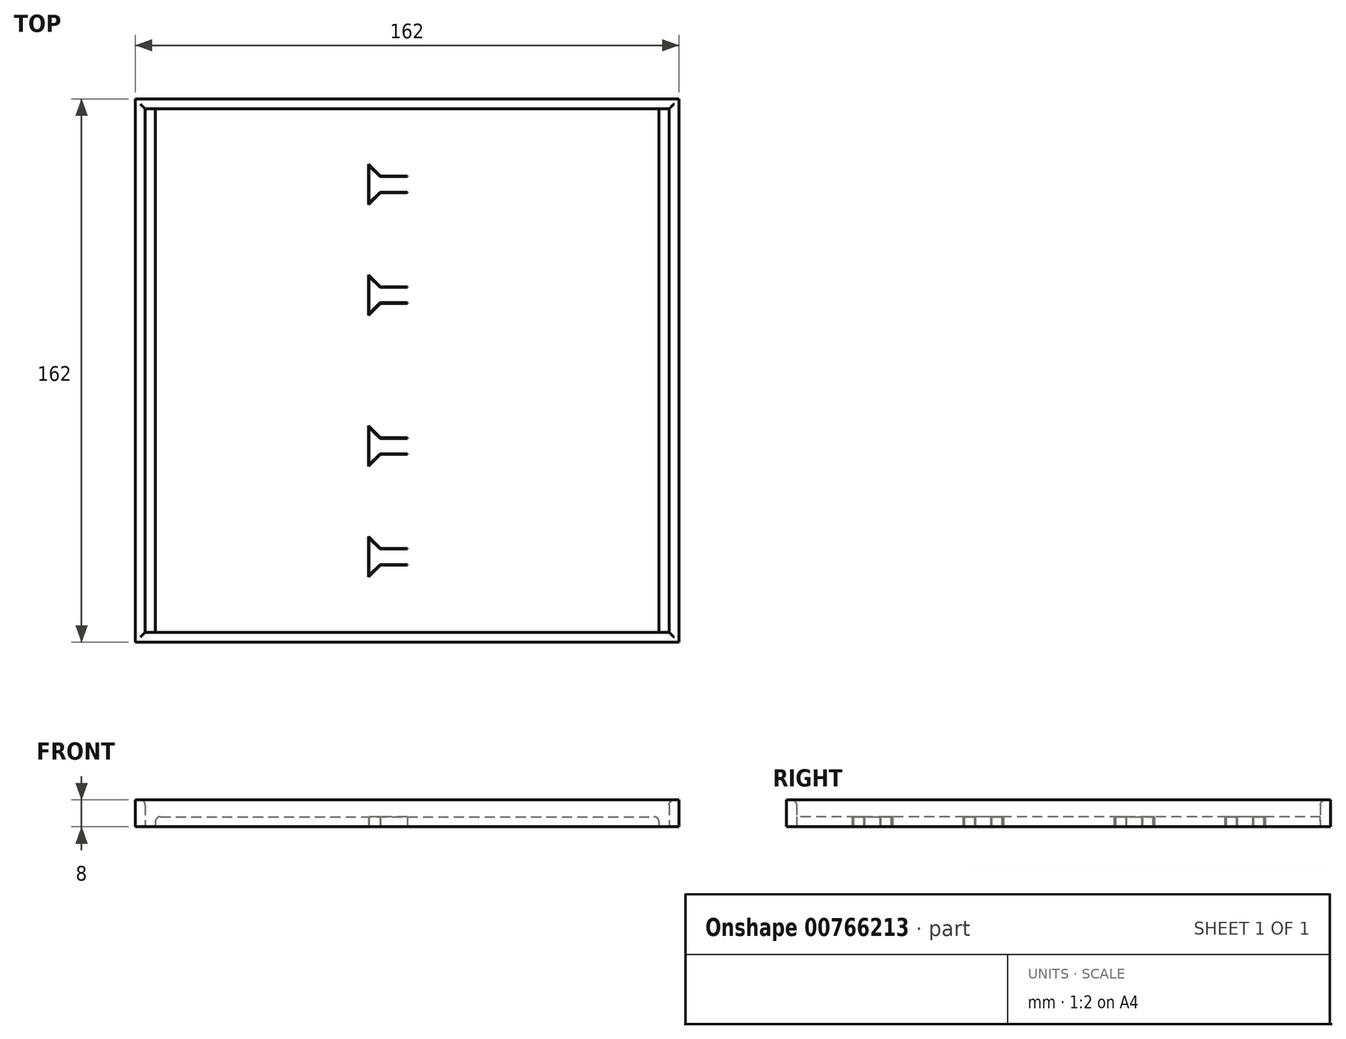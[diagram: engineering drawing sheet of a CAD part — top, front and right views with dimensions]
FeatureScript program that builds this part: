
annotation { "Feature Type Name" : "Feature", "Feature Type Description" : "" }
export const myFeature = defineFeature(function(context is Context, id is Id, definition is map)
    precondition{}
    {
        {
            var Q0;
            Q0=qCreatedBy(makeId("Top.planeOp"),FACE);
            var sketch = newSketch(context, id + "F0", { "sketchPlane" : qUnion([Q0])});
            skLineSegment(sketch, "E0.bottom", {"start": v(-39, 39) * mm, "end": v(39, 39) * mm});
            skLineSegment(sketch, "E0.top", {"start": v(-39, -39) * mm, "end": v(39, -39) * mm, "construction": true});
            skLineSegment(sketch, "E0.left", {"start": v(-39, 39) * mm, "end": v(-39, -39) * mm});
            skLineSegment(sketch, "E0.right", {"start": v(39, 39) * mm, "end": v(39, -39) * mm, "construction": true});
            skPoint(sketch, "E0.middle", {"position": v(0, 0) * mm});
            skLineSegment(sketch, "E1", {"start": v(-39, -39) * mm, "end": v(-42, -39) * mm, "construction": true});
            skLineSegment(sketch, "E2", {"start": v(-42, -39) * mm, "end": v(-42, 42) * mm});
            skLineSegment(sketch, "E3", {"start": v(-42, 42) * mm, "end": v(39, 42) * mm});
            skLineSegment(sketch, "E4", {"start": v(39, 42) * mm, "end": v(39, 39) * mm, "construction": true});
            skLineSegment(sketch, "E5.MirrorCS", {"start": v(-39, -117) * mm, "end": v(39, -117) * mm});
            skLineSegment(sketch, "E6.MirrorCS", {"start": v(-42, -120) * mm, "end": v(39, -120) * mm});
            skLineSegment(sketch, "E7.MirrorCS", {"start": v(-39, -117) * mm, "end": v(-39, -39) * mm});
            skLineSegment(sketch, "E8.MirrorCS", {"start": v(-42, -39) * mm, "end": v(-42, -120) * mm});
            skLineSegment(sketch, "E9.MirrorCS", {"start": v(117, -117) * mm, "end": v(117, -39) * mm});
            skLineSegment(sketch, "E10.MirrorCS", {"start": v(117, 39) * mm, "end": v(117, -39) * mm});
            skLineSegment(sketch, "E11.MirrorCS", {"start": v(120, -39) * mm, "end": v(120, 42) * mm});
            skLineSegment(sketch, "E12.MirrorCS", {"start": v(120, -39) * mm, "end": v(120, -120) * mm});
            skLineSegment(sketch, "E13.MirrorCS", {"start": v(120, 42) * mm, "end": v(39, 42) * mm});
            skLineSegment(sketch, "E14.MirrorCS", {"start": v(117, 39) * mm, "end": v(39, 39) * mm});
            skLineSegment(sketch, "E15.MirrorCS", {"start": v(117, -117) * mm, "end": v(39, -117) * mm});
            skLineSegment(sketch, "E16.MirrorCS", {"start": v(120, -120) * mm, "end": v(39, -120) * mm});
            skLineSegment(sketch, "E17", {"start": v(39, 42) * mm, "end": v(39, -120) * mm});
            skPoint(sketch, "E18", {"position": v(39, 19) * mm});
            skPoint(sketch, "E19", {"position": v(39, 14) * mm});
            skPoint(sketch, "E20", {"position": v(39, 0) * mm});
            skLineSegment(sketch, "E21", {"start": v(39, 19) * mm, "end": v(31, 19) * mm});
            skLineSegment(sketch, "E22", {"start": v(31, 19) * mm, "end": v(27.46, 22.54) * mm});
            skLineSegment(sketch, "E23", {"start": v(27.46, 22.54) * mm, "end": v(27.46, 10.46) * mm});
            skLineSegment(sketch, "E24", {"start": v(27.46, 10.46) * mm, "end": v(31, 14) * mm});
            skLineSegment(sketch, "E25", {"start": v(31, 14) * mm, "end": v(39, 14) * mm});
            skLineSegment(sketch, "E26", {"start": v(0, 0) * mm, "end": v(39, 0) * mm, "construction": true});
            skLineSegment(sketch, "E27.MirrorCS", {"start": v(31, -14) * mm, "end": v(39, -14) * mm});
            skLineSegment(sketch, "E28.MirrorCS", {"start": v(27.46, -10.46) * mm, "end": v(31, -14) * mm});
            skLineSegment(sketch, "E29.MirrorCS", {"start": v(27.46, -22.54) * mm, "end": v(27.46, -10.46) * mm});
            skLineSegment(sketch, "E30.MirrorCS", {"start": v(31, -19) * mm, "end": v(27.46, -22.54) * mm});
            skLineSegment(sketch, "E31.MirrorCS", {"start": v(39, -19) * mm, "end": v(31, -19) * mm});
            skLineSegment(sketch, "E32.MirrorCS", {"start": v(39, -59) * mm, "end": v(31, -59) * mm});
            skLineSegment(sketch, "E33.MirrorCS", {"start": v(31, -59) * mm, "end": v(27.46, -55.46) * mm});
            skLineSegment(sketch, "E34.MirrorCS", {"start": v(27.46, -55.46) * mm, "end": v(27.46, -67.54) * mm});
            skLineSegment(sketch, "E35.MirrorCS", {"start": v(27.46, -67.54) * mm, "end": v(31, -64) * mm});
            skLineSegment(sketch, "E36.MirrorCS", {"start": v(31, -64) * mm, "end": v(39, -64) * mm});
            skLineSegment(sketch, "E37.MirrorCS", {"start": v(31, -92) * mm, "end": v(39, -92) * mm});
            skLineSegment(sketch, "E38.MirrorCS", {"start": v(39, -97) * mm, "end": v(31, -97) * mm});
            skLineSegment(sketch, "E39.MirrorCS", {"start": v(31, -97) * mm, "end": v(27.46, -100.54) * mm});
            skLineSegment(sketch, "E40.MirrorCS", {"start": v(27.46, -100.54) * mm, "end": v(27.46, -88.46) * mm});
            skLineSegment(sketch, "E41.MirrorCS", {"start": v(27.46, -88.46) * mm, "end": v(31, -92) * mm});
            skLineSegment(sketch, "E42", {"start": v(-36, 39) * mm, "end": v(-36, -117) * mm});
            skLineSegment(sketch, "E43.MirrorCS", {"start": v(114, 39) * mm, "end": v(114, -117) * mm});
            skLineSegment(sketch, "E44.0", {"start": v(30.92, 14.2) * mm, "end": v(39, 14.2) * mm});
            skLineSegment(sketch, "E44.1", {"start": v(39, 18.8) * mm, "end": v(30.92, 18.8) * mm});
            skLineSegment(sketch, "E44.2", {"start": v(30.92, 18.8) * mm, "end": v(27.66, 22.05) * mm});
            skLineSegment(sketch, "E44.3", {"start": v(27.66, 22.05) * mm, "end": v(27.66, 10.95) * mm});
            skLineSegment(sketch, "E44.4", {"start": v(27.66, 10.95) * mm, "end": v(30.92, 14.2) * mm});
            skLineSegment(sketch, "E45.MirrorCS", {"start": v(30.92, -14.2) * mm, "end": v(39, -14.2) * mm});
            skLineSegment(sketch, "E46.MirrorCS", {"start": v(27.66, -10.95) * mm, "end": v(30.92, -14.2) * mm});
            skLineSegment(sketch, "E47.MirrorCS", {"start": v(27.66, -22.05) * mm, "end": v(27.66, -10.95) * mm});
            skLineSegment(sketch, "E48.MirrorCS", {"start": v(30.92, -18.8) * mm, "end": v(27.66, -22.05) * mm});
            skLineSegment(sketch, "E49.MirrorCS", {"start": v(39, -18.8) * mm, "end": v(30.92, -18.8) * mm});
            skLineSegment(sketch, "E50.MirrorCS", {"start": v(39, -59.2) * mm, "end": v(30.92, -59.2) * mm});
            skLineSegment(sketch, "E51.MirrorCS", {"start": v(30.92, -59.2) * mm, "end": v(27.66, -55.95) * mm});
            skLineSegment(sketch, "E52.MirrorCS", {"start": v(27.66, -55.95) * mm, "end": v(27.66, -67.05) * mm});
            skLineSegment(sketch, "E53.MirrorCS", {"start": v(30.92, -63.8) * mm, "end": v(39, -63.8) * mm});
            skLineSegment(sketch, "E54.MirrorCS", {"start": v(27.66, -67.05) * mm, "end": v(30.92, -63.8) * mm});
            skLineSegment(sketch, "E55.MirrorCS", {"start": v(30.92, -92.2) * mm, "end": v(39, -92.2) * mm});
            skLineSegment(sketch, "E56.MirrorCS", {"start": v(27.66, -88.95) * mm, "end": v(30.92, -92.2) * mm});
            skLineSegment(sketch, "E57.MirrorCS", {"start": v(27.66, -100.05) * mm, "end": v(27.66, -88.95) * mm});
            skLineSegment(sketch, "E58.MirrorCS", {"start": v(30.92, -96.8) * mm, "end": v(27.66, -100.05) * mm});
            skLineSegment(sketch, "E59.MirrorCS", {"start": v(39, -96.8) * mm, "end": v(30.92, -96.8) * mm});
            skSolve(sketch);
        }
        {
            var Q0;
            {var subQ1=sQuery(id+"F0.wireOp",EDGE,"E0.bottom");Q0=makeQuery(id+"F0.imprint","IMPRINT",FACE,{"disambiguationData":[TD([[makeQuery(id+"F0.imprint","IMPRINT",EDGE,{"derivedFrom":subQ1}),1.0]])]});}
            extrude(context, id + "F1", {"entities" : qUnion([Q0]), "depth" : 8 * mm, "offsetDistance" : 25 * mm});
        }
        {
            var Q0;
            {var subQ9=sQuery(id+"F0.wireOp",EDGE,"E21");Q0=makeQuery(id+"F0.imprint","IMPRINT",FACE,{"disambiguationData":[TD([[makeQuery(id+"F0.imprint","IMPRINT",EDGE,{"derivedFrom":subQ9}),-1.0]])]});}
            extrude(context, id + "F2", {"entities" : qUnion([Q0]), "operationType" : NewBodyOperationType.ADD, "depth" : 3 * mm, "offsetDistance" : 25 * mm});
        }
        {
            var Q0;
            {var subQ10=sQuery(id+"F0.wireOp",EDGE,"E43.MirrorCS");Q0=makeQuery(id+"F0.imprint","IMPRINT",FACE,{"disambiguationData":[TD([[makeQuery(id+"F0.imprint","IMPRINT",EDGE,{"derivedFrom":subQ10}),-1.0]])]});}
            var Q1;
            {var subQ6=sQuery(id+"F0.wireOp",EDGE,"E9.MirrorCS");Q1=makeQuery(id+"F0.imprint","IMPRINT",FACE,{"disambiguationData":[TD([[makeQuery(id+"F0.imprint","IMPRINT",EDGE,{"derivedFrom":subQ6}),-1.0]])]});}
            var Q2;
            {var subQ0=sQuery(id+"F0.wireOp",EDGE,"E55.MirrorCS");Q2=makeQuery(id+"F0.imprint","IMPRINT",FACE,{"disambiguationData":[TD([[makeQuery(id+"F0.imprint","IMPRINT",EDGE,{"derivedFrom":subQ0}),-1.0]])]});}
            var Q3;
            {var subQ0=sQuery(id+"F0.wireOp",EDGE,"E50.MirrorCS");Q3=makeQuery(id+"F0.imprint","IMPRINT",FACE,{"disambiguationData":[TD([[makeQuery(id+"F0.imprint","IMPRINT",EDGE,{"derivedFrom":subQ0}),1.0]])]});}
            var Q4;
            {var subQ0=sQuery(id+"F0.wireOp",EDGE,"E45.MirrorCS");Q4=makeQuery(id+"F0.imprint","IMPRINT",FACE,{"disambiguationData":[TD([[makeQuery(id+"F0.imprint","IMPRINT",EDGE,{"derivedFrom":subQ0}),-1.0]])]});}
            var Q5;
            {var subQ1=sQuery(id+"F0.wireOp",EDGE,"E44.0");Q5=makeQuery(id+"F0.imprint","IMPRINT",FACE,{"disambiguationData":[TD([[makeQuery(id+"F0.imprint","IMPRINT",EDGE,{"derivedFrom":subQ1}),1.0]])]});}
            extrude(context, id + "F3", {"entities" : qUnion([Q0, Q1, Q2, Q3, Q4, Q5]), "depth" : 3 * mm, "offsetDistance" : 25 * mm});
        }
        {
            var Q0;
            {var subQ6=sQuery(id+"F0.wireOp",EDGE,"E9.MirrorCS");Q0=makeQuery(id+"F0.imprint","IMPRINT",FACE,{"disambiguationData":[TD([[makeQuery(id+"F0.imprint","IMPRINT",EDGE,{"derivedFrom":subQ6}),-1.0]])]});}
            extrude(context, id + "F4", {"entities" : qUnion([Q0]), "operationType" : NewBodyOperationType.ADD, "depth" : 8 * mm, "offsetDistance" : 25 * mm});
        }
        {
            var Q0;
            Q0=makeQuery(id+"F1.opExtrude","CAP_EDGE",EDGE,{"disambiguationData":[OSD([sQuery(id+"F0.wireOp",EDGE,"E0.bottom")])],"isStart":false});
            var Q1;
            Q1=makeQuery(id+"F4.opExtrude","CAP_EDGE",EDGE,{"disambiguationData":[OSD([sQuery(id+"F0.wireOp",EDGE,"E14.MirrorCS")])],"isStart":false});
            var Q2;
            Q2=makeQuery(id+"F4.opExtrude","CAP_EDGE",EDGE,{"disambiguationData":[OSD([sQuery(id+"F0.wireOp",EDGE,"E9.MirrorCS"),sQuery(id+"F0.wireOp",EDGE,"E10.MirrorCS")])],"isStart":false});
            var Q3;
            Q3=makeQuery(id+"F4.opExtrude","CAP_EDGE",EDGE,{"disambiguationData":[OSD([sQuery(id+"F0.wireOp",EDGE,"E15.MirrorCS")])],"isStart":false});
            var Q4;
            Q4=makeQuery(id+"F1.opExtrude","CAP_EDGE",EDGE,{"disambiguationData":[OSD([sQuery(id+"F0.wireOp",EDGE,"E5.MirrorCS")])],"isStart":false});
            var Q5;
            Q5=makeQuery(id+"F1.opExtrude","CAP_EDGE",EDGE,{"disambiguationData":[OSD([sQuery(id+"F0.wireOp",EDGE,"E0.left"),sQuery(id+"F0.wireOp",EDGE,"E7.MirrorCS")])],"isStart":false});
            var Q6;
            Q6=makeQuery(id+"F2.opExtrude","CAP_EDGE",EDGE,{"disambiguationData":[OSD([sQuery(id+"F0.wireOp",EDGE,"E42")])],"isStart":false});
            var Q7;
            Q7=makeQuery(id+"F3.opExtrude","CAP_EDGE",EDGE,{"disambiguationData":[OSD([sQuery(id+"F0.wireOp",EDGE,"E43.MirrorCS")])],"isStart":false});
            fillet(context, id + "F5", {"entities" : qUnion([Q0, Q1, Q2, Q3, Q4, Q5, Q6, Q7]), "radius" : 1.5 * mm, "tangentPropagation" : true, "allowEdgeOverflow" : false});
        }
    });
